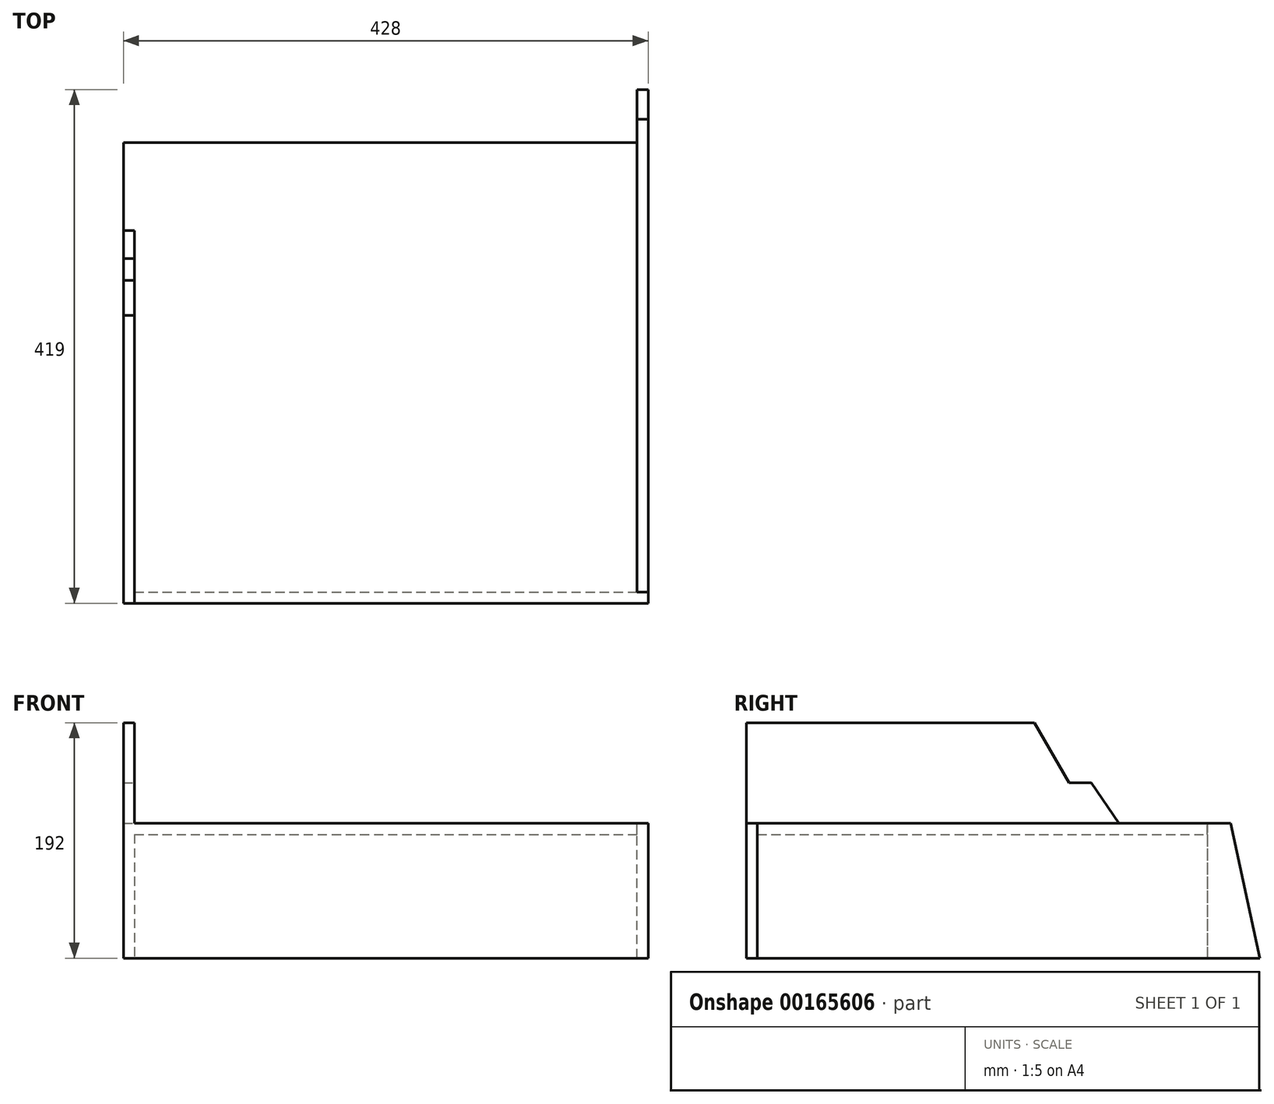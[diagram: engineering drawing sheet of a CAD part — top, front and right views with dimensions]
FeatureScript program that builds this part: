
annotation { "Feature Type Name" : "Feature", "Feature Type Description" : "" }
export const myFeature = defineFeature(function(context is Context, id is Id, definition is map)
    precondition{}
    {
        {
            var Q0;
            Q0=qCreatedBy(makeId("Top.planeOp"),FACE);
            var sketch = newSketch(context, id + "F0", { "sketchPlane" : qUnion([Q0])});
            skLineSegment(sketch, "E0.bottom", {"start": v(0, 0) * mm, "end": v(410, 0) * mm});
            skLineSegment(sketch, "E0.top", {"start": v(0, 367) * mm, "end": v(410, 367) * mm});
            skLineSegment(sketch, "E0.left", {"start": v(0, 0) * mm, "end": v(0, 367) * mm});
            skLineSegment(sketch, "E0.right", {"start": v(410, 0) * mm, "end": v(410, 367) * mm});
            skLineSegment(sketch, "E1.bottom", {"start": v(0, 0) * mm, "end": v(419, 0) * mm});
            skLineSegment(sketch, "E1.top", {"start": v(0, -9) * mm, "end": v(419, -9) * mm});
            skLineSegment(sketch, "E1.left", {"start": v(0, 0) * mm, "end": v(0, -9) * mm});
            skLineSegment(sketch, "E1.right", {"start": v(419, 0) * mm, "end": v(419, -9) * mm});
            skSolve(sketch);
        }
        {
            var Q0;
            Q0=makeQuery(id+"F0.imprint","IMPRINT",FACE,{"disambiguationData":[TD([[makeQuery(id+"F0.imprint","IMPRINT",EDGE,{"derivedFrom":sQuery(id+"F0.wireOp",EDGE,"E0.top")}),-1.0]])]});
            extrude(context, id + "F1", {"entities" : qUnion([Q0]), "oppositeDirection" : true, "depth" : 9 * mm});
        }
        {
            var Q0;
            Q0=makeQuery(id+"F0.imprint","IMPRINT",FACE,{"disambiguationData":[TD([[makeQuery(id+"F0.imprint","IMPRINT",EDGE,{"derivedFrom":sQuery(id+"F0.wireOp",EDGE,"E1.top")}),1.0]])]});
            extrude(context, id + "F2", {"entities" : qUnion([Q0]), "operationType" : NewBodyOperationType.ADD, "oppositeDirection" : true, "depth" : 110 * mm});
        }
        {
            var Q0;
            Q0=makeQuery(id+"F2.opExtrude","SWEPT_FACE",FACE,{"disambiguationData":[OSD([sQuery(id+"F0.wireOp",EDGE,"E1.right")])]});
            var sketch = newSketch(context, id + "F3", { "sketchPlane" : qUnion([Q0])});
            skLineSegment(sketch, "E2", {"start": v(0, 0) * mm, "end": v(386, 0) * mm});
            skLineSegment(sketch, "E3", {"start": v(386, 0) * mm, "end": v(410, -110) * mm});
            skLineSegment(sketch, "E4", {"start": v(410, -110) * mm, "end": v(0, -110) * mm});
            skLineSegment(sketch, "E5", {"start": v(0, -110) * mm, "end": v(0, 0) * mm});
            skSolve(sketch);
        }
        {
            var Q0;
            Q0=makeQuery(id+"F3.imprint","IMPRINT",FACE,{"disambiguationData":[TD([[makeQuery(id+"F3.imprint","IMPRINT",EDGE,{"derivedFrom":sQuery(id+"F3.wireOp",EDGE,"E2")}),-1.0]])]});
            extrude(context, id + "F4", {"entities" : qUnion([Q0]), "oppositeDirection" : true, "depth" : 9 * mm});
        }
        {
            var Q0;
            Q0=makeQuery(id+"F2.boolean.opBoolean","MERGE",FACE,{"derivedFrom":[makeQuery(id+"F1.opExtrude","SWEPT_FACE",FACE,{"disambiguationData":[OSD([sQuery(id+"F0.wireOp",EDGE,"E0.left")])]}),makeQuery(id+"F2.opExtrude","SWEPT_FACE",FACE,{"disambiguationData":[OSD([sQuery(id+"F0.wireOp",EDGE,"E1.left")])]})]});
            var sketch = newSketch(context, id + "F5", { "sketchPlane" : qUnion([Q0])});
            skLineSegment(sketch, "E6", {"start": v(9, -110) * mm, "end": v(9, 82) * mm});
            skLineSegment(sketch, "E7", {"start": v(9, 82) * mm, "end": v(-226, 82) * mm});
            skLineSegment(sketch, "E8", {"start": v(-226, 82) * mm, "end": v(-254.32, 32.95) * mm});
            skLineSegment(sketch, "E9", {"start": v(-254.32, 32.95) * mm, "end": v(-272.32, 32.95) * mm});
            skLineSegment(sketch, "E10", {"start": v(-272.32, 32.95) * mm, "end": v(-295, 0) * mm});
            skLineSegment(sketch, "E11", {"start": v(-295, 0) * mm, "end": v(-367, 0) * mm});
            skLineSegment(sketch, "E12", {"start": v(-367, 0) * mm, "end": v(-367, -110) * mm});
            skLineSegment(sketch, "E13", {"start": v(-367, -110) * mm, "end": v(9, -110) * mm});
            skSolve(sketch);
        }
        {
            var Q0;
            Q0 = qSketchRegion(id + "F5", true);
            extrude(context, id + "F6", {"entities" : qUnion([Q0]), "operationType" : NewBodyOperationType.ADD, "depth" : 9 * mm});
        }
    });
